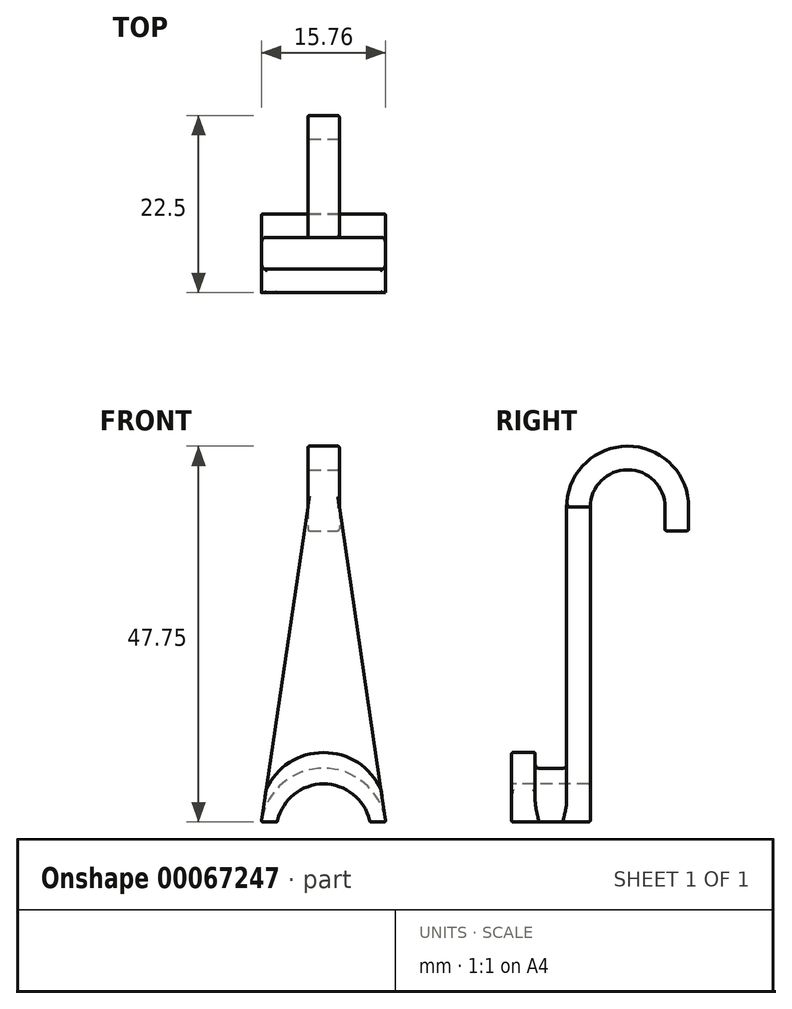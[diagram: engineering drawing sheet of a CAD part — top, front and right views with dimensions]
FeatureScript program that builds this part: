
annotation { "Feature Type Name" : "Feature", "Feature Type Description" : "" }
export const myFeature = defineFeature(function(context is Context, id is Id, definition is map)
    precondition{}
    {
        {
            var Q0;
            Q0=qCreatedBy(makeId("Front.planeOp"),FACE);
            var sketch = newSketch(context, id + "F0", { "sketchPlane" : qUnion([Q0])});
            skArc(sketch, "E0", {"start": v(7.91, 1.17) * mm, "mid": v(0, 8) * mm, "end": v(-7.91, 1.17) * mm});
            skArc(sketch, "E1.0", {"start": v(5.88, 1.17) * mm, "mid": v(0, 6) * mm, "end": v(-5.88, 1.17) * mm});
            skLineSegment(sketch, "E2", {"start": v(-2, 41.17) * mm, "end": v(-7.91, 1.17) * mm});
            skLineSegment(sketch, "E3.MirrorCS", {"start": v(2, 41.17) * mm, "end": v(7.91, 1.17) * mm});
            skLineSegment(sketch, "E4", {"start": v(-7.91, 1.17) * mm, "end": v(-5.88, 1.17) * mm});
            skLineSegment(sketch, "E5.trimOffspring", {"start": v(5.88, 1.17) * mm, "end": v(7.91, 1.17) * mm});
            skLineSegment(sketch, "E6", {"start": v(-7.91, 1.17) * mm, "end": v(-7.91, 3.17) * mm});
            skLineSegment(sketch, "E7", {"start": v(7.91, 1.17) * mm, "end": v(7.91, 3.17) * mm});
            skArc(sketch, "E8", {"start": v(7.91, 3.17) * mm, "mid": v(0, 10) * mm, "end": v(-7.91, 3.17) * mm});
            skLineSegment(sketch, "E9", {"start": v(-2, 41.17) * mm, "end": v(2, 41.17) * mm});
            skPoint(sketch, "E10.orphan", {"position": v(3.99, 27.71) * mm});
            skSolve(sketch);
        }
        {
            var Q0;
            {var subQ0=sQuery(id+"F0.wireOp",EDGE,"E3.MirrorCS");var subQ1=sQuery(id+"F0.wireOp",EDGE,"E2");var subQ2=makeQuery(id+"F0.imprint","INTERSECT",VERTEX,{"derivedFrom":[subQ1,subQ0]});Q0=makeQuery(id+"F0.imprint","IMPRINT",FACE,{"disambiguationData":[TD([[makeQuery(id+"F0.imprint","IMPRINT",EDGE,{"disambiguationData":[TD([[subQ2,-1.0]])],"derivedFrom":subQ1}),1.0]])]});}
            var Q1;
            {var subQ0=sQuery(id+"F0.wireOp",EDGE,"E0");Q1=makeQuery(id+"F0.imprint","IMPRINT",FACE,{"disambiguationData":[TD([[makeQuery(id+"F0.imprint","IMPRINT",EDGE,{"derivedFrom":subQ0}),-1.0]])]});}
            var Q2;
            Q2=makeQuery(id+"F0.imprint","IMPRINT",FACE,{"disambiguationData":[TD([[makeQuery(id+"F0.imprint","IMPRINT",EDGE,{"derivedFrom":sQuery(id+"F0.wireOp",EDGE,"E0")}),1.0]])]});
            extrude(context, id + "F1", {"entities" : qUnion([Q0, Q1, Q2]), "oppositeDirection" : true, "depth" : 3 * mm});
        }
        {
            var Q0;
            Q0=makeQuery(id+"F0.imprint","IMPRINT",FACE,{"disambiguationData":[TD([[makeQuery(id+"F0.imprint","IMPRINT",EDGE,{"derivedFrom":sQuery(id+"F0.wireOp",EDGE,"E0")}),1.0]])]});
            var Q1;
            {var subQ0=sQuery(id+"F0.wireOp",EDGE,"E0");Q1=makeQuery(id+"F0.imprint","IMPRINT",FACE,{"disambiguationData":[TD([[makeQuery(id+"F0.imprint","IMPRINT",EDGE,{"derivedFrom":subQ0}),-1.0]])]});}
            extrude(context, id + "F2", {"entities" : qUnion([Q0, Q1]), "operationType" : NewBodyOperationType.ADD, "depth" : 7 * mm});
        }
        {
            var Q0;
            {var subQ0=sQuery(id+"F0.wireOp",EDGE,"E0");Q0=makeQuery(id+"F0.imprint","IMPRINT",FACE,{"disambiguationData":[TD([[makeQuery(id+"F0.imprint","IMPRINT",EDGE,{"derivedFrom":subQ0}),-1.0]])]});}
            extrude(context, id + "F3", {"entities" : qUnion([Q0]), "operationType" : NewBodyOperationType.REMOVE, "depth" : 4 * mm});
        }
        {
            var Q0;
            Q0=qCreatedBy(makeId("Right.planeOp"),FACE);
            var sketch = newSketch(context, id + "F4", { "sketchPlane" : qUnion([Q0])});
            skArc(sketch, "E11", {"start": v(12.5, 41.17) * mm, "mid": v(7.75, 45.92) * mm, "end": v(3, 41.17) * mm});
            skArc(sketch, "E12", {"start": v(15.5, 41.17) * mm, "mid": v(7.75, 48.92) * mm, "end": v(0, 41.17) * mm});
            skLineSegment(sketch, "E13", {"start": v(7.75, 41.17) * mm, "end": v(15.5, 41.17) * mm, "construction": true});
            skLineSegment(sketch, "E14", {"start": v(3, 27.07) * mm, "end": v(3, 2.46) * mm, "construction": true});
            skLineSegment(sketch, "E15.top", {"start": v(15.5, 38.17) * mm, "end": v(12.5, 38.17) * mm});
            skLineSegment(sketch, "E15.left", {"start": v(15.5, 41.17) * mm, "end": v(15.5, 38.17) * mm});
            skLineSegment(sketch, "E15.right", {"start": v(12.5, 41.17) * mm, "end": v(12.5, 38.17) * mm});
            skLineSegment(sketch, "E16", {"start": v(3, 41.17) * mm, "end": v(0, 41.17) * mm});
            skSolve(sketch);
        }
        {
            var Q0;
            Q0=makeQuery(id+"F4.imprint","IMPRINT",FACE,{"disambiguationData":[TD([[makeQuery(id+"F4.imprint","IMPRINT",EDGE,{"derivedFrom":sQuery(id+"F4.wireOp",EDGE,"E11")}),-1.0]])]});
            var Q1;
            {var subQ0=sQuery(id+"F0.wireOp",EDGE,"E9");var subQ5=sQuery(id+"F0.wireOp",EDGE,"E2");Q1=makeQuery(id+"F3.boolean.opBoolean","SPLIT",FACE,{"disambiguationData":[TD([makeQuery(id+"F1.opExtrude","SWEPT_FACE",FACE,{"disambiguationData":[OSD([subQ0])]})])],"derivedFrom":makeQuery(id+"F2.boolean.opBoolean","MERGE",FACE,{"derivedFrom":[makeQuery(id+"F1.opExtrude","SWEPT_FACE",FACE,{"disambiguationData":[OSD([subQ5])]}),makeQuery(id+"F2.opExtrude","SWEPT_FACE",FACE,{"disambiguationData":[OSD([subQ5])]})]})});}
            var Q2;
            {var subQ0=sQuery(id+"F0.wireOp",EDGE,"E9");var subQ3=sQuery(id+"F0.wireOp",EDGE,"E3.MirrorCS");Q2=makeQuery(id+"F3.boolean.opBoolean","SPLIT",FACE,{"disambiguationData":[TD([makeQuery(id+"F1.opExtrude","SWEPT_FACE",FACE,{"disambiguationData":[OSD([subQ0])]})])],"derivedFrom":makeQuery(id+"F2.boolean.opBoolean","MERGE",FACE,{"derivedFrom":[makeQuery(id+"F1.opExtrude","SWEPT_FACE",FACE,{"disambiguationData":[OSD([subQ3])]}),makeQuery(id+"F2.opExtrude","SWEPT_FACE",FACE,{"disambiguationData":[OSD([subQ3])]})]})});}
            extrude(context, id + "F5", {"entities" : qUnion([Q0]), "operationType" : NewBodyOperationType.ADD, "oppositeDirection" : true, "endBoundEntityFace" : qUnion([Q1]), "depth" : 2 * mm, "hasSecondDirection" : true, "secondDirectionOppositeDirection" : false, "secondDirectionBoundEntityFace" : qUnion([Q2]), "secondDirectionDepth" : 2 * mm});
        }
        {
            var Q0;
            {var subQ0=sQuery(id+"F0.wireOp",EDGE,"E4");Q0=makeQuery(id+"F2.boolean.opBoolean","MERGE",FACE,{"derivedFrom":[makeQuery(id+"F1.opExtrude","SWEPT_FACE",FACE,{"disambiguationData":[OSD([subQ0])]}),makeQuery(id+"F2.opExtrude","SWEPT_FACE",FACE,{"disambiguationData":[OSD([subQ0])]})]});}
            var Q1;
            {var subQ0=sQuery(id+"F0.wireOp",EDGE,"E5.trimOffspring");Q1=makeQuery(id+"F2.boolean.opBoolean","MERGE",FACE,{"derivedFrom":[makeQuery(id+"F1.opExtrude","SWEPT_FACE",FACE,{"disambiguationData":[OSD([subQ0])]}),makeQuery(id+"F2.opExtrude","SWEPT_FACE",FACE,{"disambiguationData":[OSD([subQ0])]})]});}
            var Q2;
            Q2=makeQuery(id+"F5.opExtrude","SWEPT_FACE",FACE,{"disambiguationData":[OSD([sQuery(id+"F4.wireOp",EDGE,"E15.top")])]});
            var Q3;
            Q3=makeQuery(id+"F5.opExtrude","SWEPT_FACE",FACE,{"disambiguationData":[OSD([sQuery(id+"F4.wireOp",EDGE,"E12")])]});
            var Q4;
            Q4=makeQuery(id+"F5.opExtrude","SWEPT_FACE",FACE,{"disambiguationData":[OSD([sQuery(id+"F4.wireOp",EDGE,"E11")])]});
            var Q5;
            Q5=makeQuery(id+"F1.opExtrude","CAP_EDGE",EDGE,{"disambiguationData":[OSD([sQuery(id+"F0.wireOp",EDGE,"E2")])],"isStart":false});
            var Q6;
            Q6=makeQuery(id+"F1.opExtrude","CAP_EDGE",EDGE,{"disambiguationData":[OSD([sQuery(id+"F0.wireOp",EDGE,"E3.MirrorCS")])],"isStart":false});
            var Q7;
            Q7=makeQuery(id+"F1.opExtrude","CAP_EDGE",EDGE,{"disambiguationData":[OSD([sQuery(id+"F0.wireOp",EDGE,"E1.0")])],"isStart":false});
            var Q8;
            Q8=makeQuery(id+"F2.opExtrude","SWEPT_FACE",FACE,{"disambiguationData":[OSD([sQuery(id+"F0.wireOp",EDGE,"E8")])]});
            fillet(context, id + "F6", {"entities" : qUnion([Q0, Q1, Q2, Q3, Q4, Q5, Q6, Q7, Q8]), "radius" : 0.2 * mm, "tangentPropagation" : true, "allowEdgeOverflow" : false});
        }
        {
            var Q0;
            Q0=makeQuery(id+"F3.boolean.opBoolean","COPY",EDGE,{"derivedFrom":makeQuery(id+"F3.opExtrude","CAP_EDGE",EDGE,{"disambiguationData":[OSD([sQuery(id+"F0.wireOp",EDGE,"E0")])],"isStart":true})});
            var Q1;
            Q1=makeQuery(id+"F3.boolean.opBoolean","COPY",EDGE,{"derivedFrom":makeQuery(id+"F3.opExtrude","CAP_EDGE",EDGE,{"disambiguationData":[OSD([sQuery(id+"F0.wireOp",EDGE,"E0")])],"isStart":false})});
            fillet(context, id + "F7", {"entities" : qUnion([Q0, Q1]), "radius" : 0.5 * mm, "tangentPropagation" : true, "allowEdgeOverflow" : false});
        }
    });
